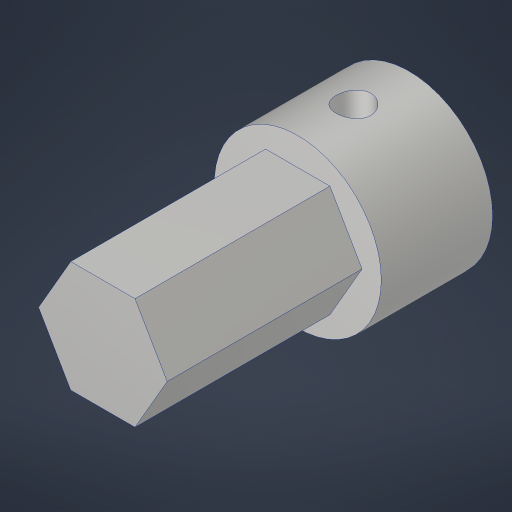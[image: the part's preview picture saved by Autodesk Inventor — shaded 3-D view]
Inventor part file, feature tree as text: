
AUTODESK INVENTOR PART (.ipt)
format: ipt  version: 2023.4 (Build 274418000, 418)  size: 187,392 bytes
history: native  units: in
note: dims shown in document units (in); Inventor stores cm internally (conversion verified against a paired STEP export)
features: sketch x3, extrude x2, hole x1
ambient origin geometry x8: Origin, YZ Plane, XZ Plane, XY Plane, X Axis, Y Axis, Z Axis, Center Point
bodies: Solid1 (feature_tree)
feature tree (6):
  extrude  "Extrusion1"  Depth=1.375in TaperAngle=0.0deg
  extrude  "Extrusion2"  Depth=0.875in TaperAngle=0.0deg
  hole  "Hole1"  [1 undecoded]
  sketch  "Sketch1"  dims[d0=0.75in d1=1.375in d2=0.0in]
  sketch  "Sketch2"  dims[d3=0.5in d4=0.875in d5=0.0in]
  sketch  "Sketch3"  dims[d6=0.25in d7=0.156in d8=0.38in d9=0.119in d10=0.25in d11=0.5635in d12=1.0in d13=0.8108in]
note: 1 required parameter value undecoded (feature->parameter linkage not recoverable at this tier; creation-order binding heuristic only, values carry confidence <= 0.55)
